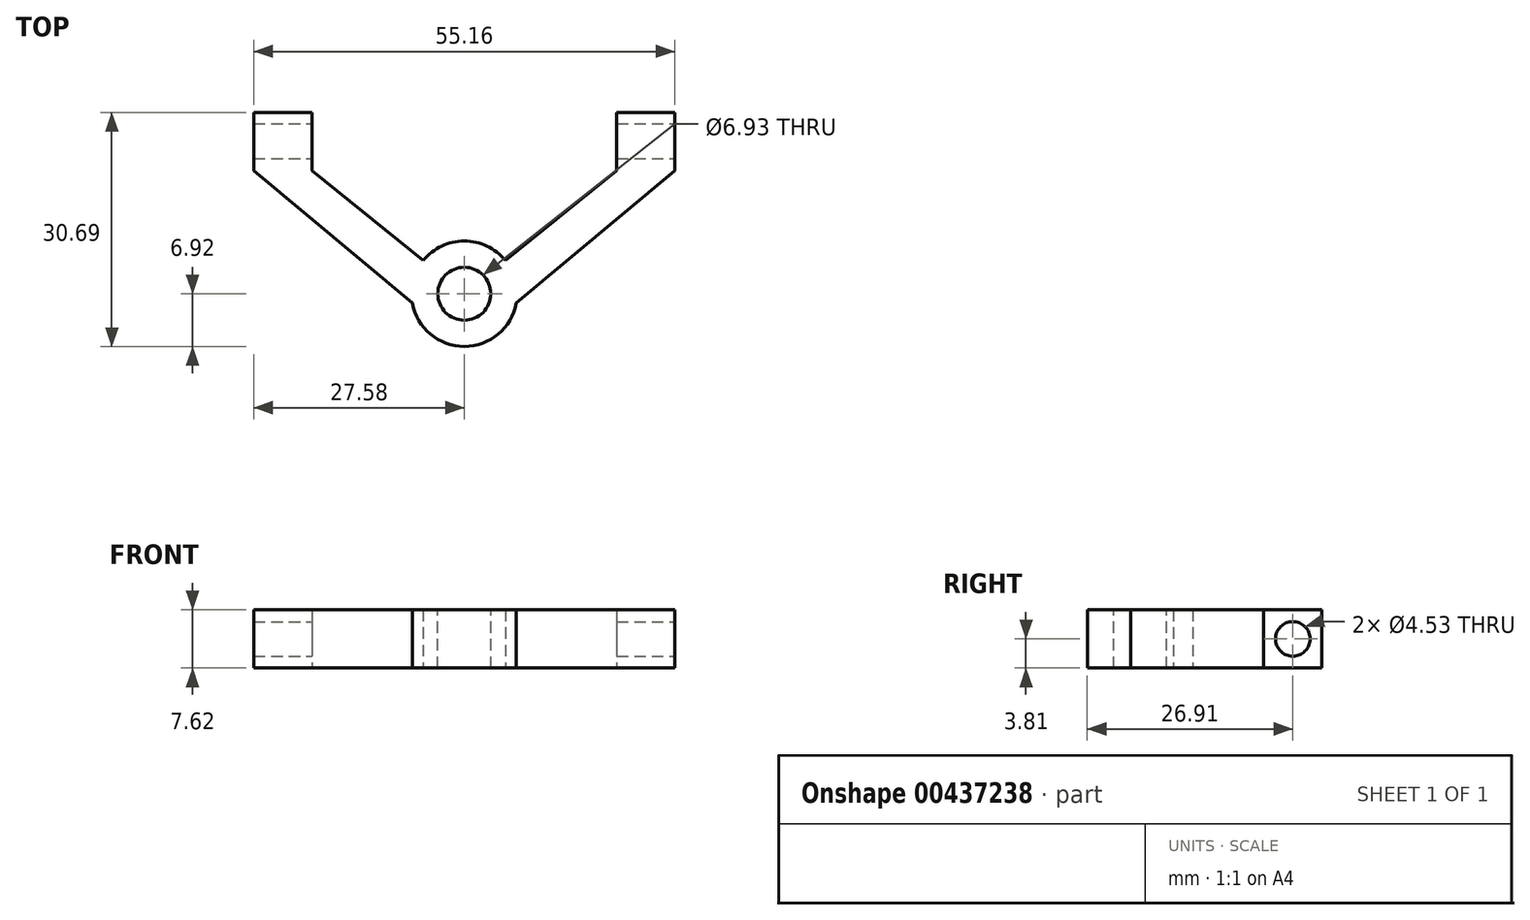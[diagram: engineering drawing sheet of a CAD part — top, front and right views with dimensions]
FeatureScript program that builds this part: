
annotation { "Feature Type Name" : "Feature", "Feature Type Description" : "" }
export const myFeature = defineFeature(function(context is Context, id is Id, definition is map)
    precondition{}
    {
        {
            var Q0;
            Q0=qCreatedBy(makeId("Top.planeOp"),FACE);
            var sketch = newSketch(context, id + "F0", { "sketchPlane" : qUnion([Q0])});
            skCircle(sketch, "E0", {"center": v(0, 0) * mm, "radius": 6.92 * mm});
            skLineSegment(sketch, "E1.bottom", {"start": v(-27.58, 16.15) * mm, "end": v(-19.96, 16.15) * mm});
            skLineSegment(sketch, "E1.top", {"start": v(-27.58, 23.77) * mm, "end": v(-19.96, 23.77) * mm});
            skLineSegment(sketch, "E1.left", {"start": v(-27.58, 16.15) * mm, "end": v(-27.58, 23.77) * mm});
            skLineSegment(sketch, "E1.right", {"start": v(-19.96, 16.15) * mm, "end": v(-19.96, 23.77) * mm});
            skLineSegment(sketch, "E2", {"start": v(0, -6.92) * mm, "end": v(-27.58, 16.15) * mm});
            skLineSegment(sketch, "E3", {"start": v(-19.96, 16.15) * mm, "end": v(0, 0) * mm});
            skLineSegment(sketch, "E4.MirrorCS", {"start": v(19.96, 16.15) * mm, "end": v(19.96, 23.77) * mm});
            skLineSegment(sketch, "E5.MirrorCS", {"start": v(27.58, 16.15) * mm, "end": v(19.96, 16.15) * mm});
            skLineSegment(sketch, "E6.MirrorCS", {"start": v(19.96, 16.15) * mm, "end": v(0, 0) * mm});
            skLineSegment(sketch, "E7.MirrorCS", {"start": v(27.58, 23.77) * mm, "end": v(19.96, 23.77) * mm});
            skLineSegment(sketch, "E8.MirrorCS", {"start": v(27.58, 16.15) * mm, "end": v(27.58, 23.77) * mm});
            skLineSegment(sketch, "E9.MirrorCS", {"start": v(0, -6.92) * mm, "end": v(27.58, 16.15) * mm});
            skSolve(sketch);
        }
        {
            var Q0;
            Q0=makeQuery(id+"F0.imprint","IMPRINT",FACE,{"disambiguationData":[TD([[makeQuery(id+"F0.imprint","IMPRINT",EDGE,{"derivedFrom":sQuery(id+"F0.wireOp",EDGE,"E1.bottom")}),1.0]])]});
            var Q1;
            Q1=makeQuery(id+"F0.imprint","IMPRINT",FACE,{"disambiguationData":[TD([[makeQuery(id+"F0.imprint","IMPRINT",EDGE,{"derivedFrom":sQuery(id+"F0.wireOp",EDGE,"E5.MirrorCS")}),-1.0]])]});
            var Q2;
            {var subQ5=sQuery(id+"F0.wireOp",EDGE,"E1.bottom");Q2=makeQuery(id+"F0.imprint","IMPRINT",FACE,{"disambiguationData":[TD([[makeQuery(id+"F0.imprint","IMPRINT",EDGE,{"derivedFrom":subQ5}),-1.0]])]});}
            var Q3;
            {var subQ5=sQuery(id+"F0.wireOp",EDGE,"E5.MirrorCS");Q3=makeQuery(id+"F0.imprint","IMPRINT",FACE,{"disambiguationData":[TD([[makeQuery(id+"F0.imprint","IMPRINT",EDGE,{"derivedFrom":subQ5}),1.0]])]});}
            var Q4;
            {var subQ0=sQuery(id+"F0.wireOp",EDGE,"E3");var subQ1=sQuery(id+"F0.wireOp",EDGE,"E0");var subQ2=makeQuery(id+"F0.imprint","INTERSECT",VERTEX,{"derivedFrom":[subQ1,subQ0]});Q4=makeQuery(id+"F0.imprint","IMPRINT",FACE,{"disambiguationData":[TD([[makeQuery(id+"F0.imprint","IMPRINT",EDGE,{"disambiguationData":[TD([[subQ2,1.0]])],"derivedFrom":subQ1}),1.0]])]});}
            var Q5;
            {var subQ0=sQuery(id+"F0.wireOp",EDGE,"E2");var subQ1=sQuery(id+"F0.wireOp",EDGE,"E0");var subQ3=makeQuery(id+"F0.imprint","INTERSECT",VERTEX,{"derivedFrom":[subQ1,subQ0]});Q5=makeQuery(id+"F0.imprint","IMPRINT",FACE,{"disambiguationData":[TD([[makeQuery(id+"F0.imprint","IMPRINT",EDGE,{"disambiguationData":[TD([[subQ3,-1.0]])],"derivedFrom":subQ1}),1.0]])]});}
            var Q6;
            {var subQ0=sQuery(id+"F0.wireOp",EDGE,"E9.MirrorCS");var subQ1=sQuery(id+"F0.wireOp",EDGE,"E0");var subQ3=makeQuery(id+"F0.imprint","INTERSECT",VERTEX,{"derivedFrom":[subQ1,subQ0]});Q6=makeQuery(id+"F0.imprint","IMPRINT",FACE,{"disambiguationData":[TD([[makeQuery(id+"F0.imprint","IMPRINT",EDGE,{"disambiguationData":[TD([[subQ3,1.0]])],"derivedFrom":subQ1}),1.0]])]});}
            var Q7;
            {var subQ1=sQuery(id+"F0.wireOp",EDGE,"E3");var subQ3=sQuery(id+"F0.wireOp",EDGE,"E0");var subQ4=makeQuery(id+"F0.imprint","INTERSECT",VERTEX,{"derivedFrom":[subQ3,subQ1]});Q7=makeQuery(id+"F0.imprint","IMPRINT",FACE,{"disambiguationData":[TD([[makeQuery(id+"F0.imprint","IMPRINT",EDGE,{"disambiguationData":[TD([[subQ4,-1.0]])],"derivedFrom":subQ3}),1.0]])]});}
            extrude(context, id + "F1", {"entities" : qUnion([Q0, Q1, Q2, Q3, Q4, Q5, Q6, Q7]), "endBound" : BoundingType.SYMMETRIC, "depth" : 7.62 * mm});
        }
        {
            var Q0;
            Q0=qCreatedBy(makeId("Right.planeOp"),FACE);
            var sketch = newSketch(context, id + "F2", { "sketchPlane" : qUnion([Q0])});
            skCircle(sketch, "E10", {"center": v(20, 0) * mm, "radius": 2.26 * mm});
            skSolve(sketch);
        }
        {
            var Q0;
            Q0 = qSketchRegion(id + "F2", true);
            extrude(context, id + "F3", {"entities" : qUnion([Q0]), "operationType" : NewBodyOperationType.REMOVE, "endBound" : BoundingType.SYMMETRIC, "oppositeDirection" : true, "depth" : 57.4 * mm});
        }
        {
            var Q0;
            Q0=qCreatedBy(makeId("Top.planeOp"),FACE);
            var sketch = newSketch(context, id + "F4", { "sketchPlane" : qUnion([Q0])});
            skCircle(sketch, "E11", {"center": v(0, 0) * mm, "radius": 3.47 * mm});
            skSolve(sketch);
        }
        {
            var Q0;
            Q0 = qSketchRegion(id + "F4", true);
            extrude(context, id + "F5", {"entities" : qUnion([Q0]), "operationType" : NewBodyOperationType.REMOVE, "endBound" : BoundingType.SYMMETRIC, "oppositeDirection" : true, "depth" : 12.2 * mm});
        }
    });
